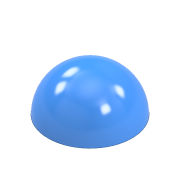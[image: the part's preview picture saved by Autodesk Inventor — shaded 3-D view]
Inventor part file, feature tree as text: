
AUTODESK INVENTOR PART (.ipt)
format: ipt  version: 2020 (Build 240168000, 168)  size: 110,080 bytes
history: native  units: mm
features: sketch x2, revolve x1, extrude x1
ambient origin geometry x8: Origin, YZ Plane, XZ Plane, XY Plane, X Axis, Y Axis, Z Axis, Center Point
bodies: Solid1 (feature_tree)
feature tree (4):
  revolve  "Revolution1"  [1 undecoded]
  extrude  "Extrusion1"  [1 undecoded]
  sketch  "Sketch1"  dims[d0=61.959188mm d1=30.5mm d2=0.0mm]
  sketch  "Sketch2"
note: 2 required parameter values undecoded (feature->parameter linkage not recoverable at this tier; creation-order binding heuristic only, values carry confidence <= 0.55)